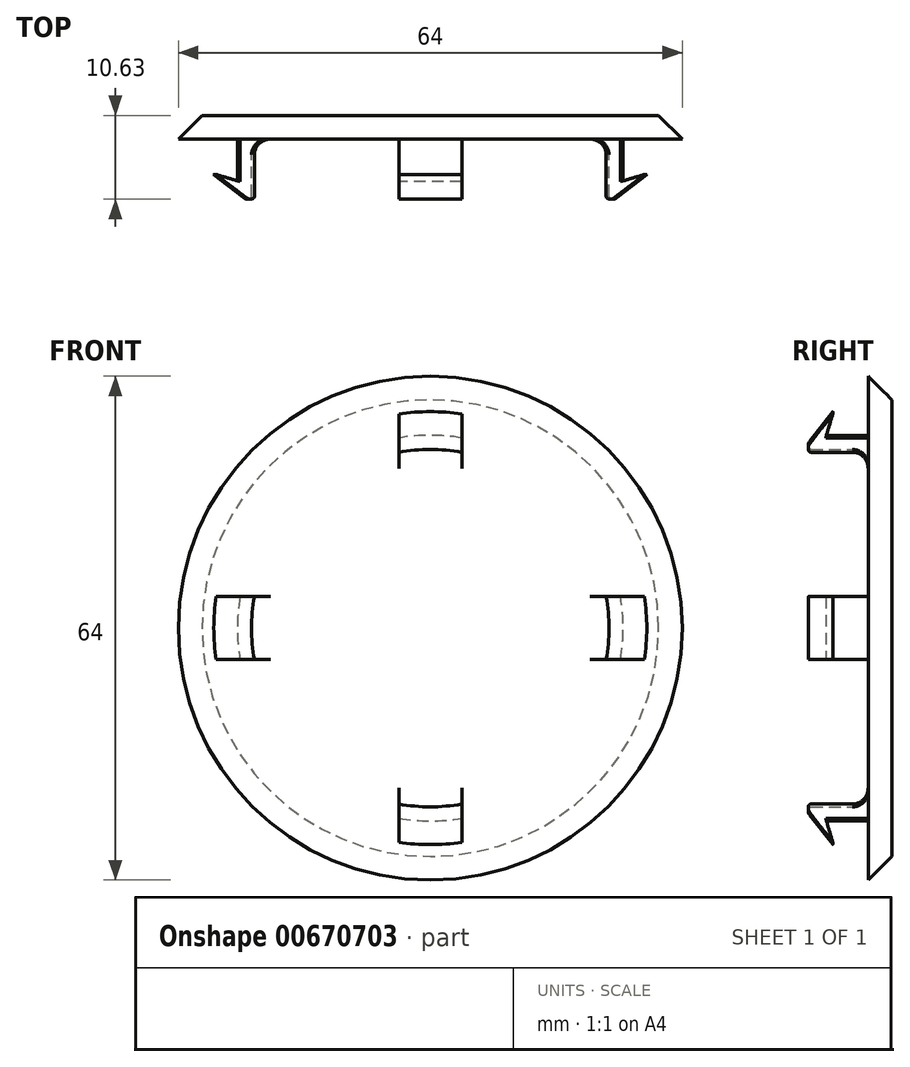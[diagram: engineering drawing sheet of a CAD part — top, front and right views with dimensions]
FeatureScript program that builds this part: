
annotation { "Feature Type Name" : "Feature", "Feature Type Description" : "" }
export const myFeature = defineFeature(function(context is Context, id is Id, definition is map)
    precondition{}
    {
        {
            var Q0;
            Q0=qCreatedBy(makeId("Top.planeOp"),FACE);
            var sketch = newSketch(context, id + "F0", { "sketchPlane" : qUnion([Q0])});
            skLineSegment(sketch, "E0", {"start": v(0, 3) * mm, "end": v(29, 3) * mm});
            skLineSegment(sketch, "E1", {"start": v(29, 3) * mm, "end": v(32, 0) * mm});
            skLineSegment(sketch, "E2", {"start": v(32, 0) * mm, "end": v(24.5, 0) * mm});
            skLineSegment(sketch, "E3", {"start": v(22.7, -7.28) * mm, "end": v(22.7, -2) * mm});
            skLineSegment(sketch, "E4", {"start": v(20.7, 0) * mm, "end": v(0, 0) * mm});
            skLineSegment(sketch, "E5", {"start": v(24.5, 0) * mm, "end": v(24.5, -3) * mm});
            skPoint(sketch, "E6.visualSharp", {"position": v(22.7, 0) * mm});
            skArc(sketch, "E6.filletArc", {"start": v(22.7, -2) * mm, "mid": v(22.11, -0.59) * mm, "end": v(20.7, 0) * mm});
            skLineSegment(sketch, "E7", {"start": v(67.9, -5) * mm, "end": v(-20.59, -5) * mm, "construction": true});
            skLineSegment(sketch, "E8", {"start": v(27.5, -4.5) * mm, "end": v(23.7, -7.45) * mm});
            skLineSegment(sketch, "E9", {"start": v(24.5, -5.4) * mm, "end": v(27.5, -4.5) * mm});
            skLineSegment(sketch, "E10", {"start": v(24.5, -3) * mm, "end": v(24.5, -5.4) * mm});
            skLineSegment(sketch, "E11", {"start": v(0, 3) * mm, "end": v(0, 0) * mm});
            skLineSegment(sketch, "E12", {"start": v(0, 22.26) * mm, "end": v(0, -28.78) * mm, "construction": true});
            skArc(sketch, "E13", {"start": v(23.7, -7.45) * mm, "mid": v(23.3, -7.62) * mm, "end": v(22.88, -7.56) * mm});
            skPoint(sketch, "E14.visualSharp", {"position": v(22.7, -7.45) * mm});
            skArc(sketch, "E14.filletArc", {"start": v(22.7, -7.28) * mm, "mid": v(22.75, -7.45) * mm, "end": v(22.88, -7.56) * mm});
            skSolve(sketch);
        }
        {
            var Q0;
            Q0=makeQuery(id+"F0.imprint","IMPRINT",FACE,{"disambiguationData":[TD([[makeQuery(id+"F0.imprint","IMPRINT",EDGE,{"derivedFrom":sQuery(id+"F0.wireOp",EDGE,"E0")}),-1.0]])]});
            var Q1;
            Q1=sQuery(id+"F0.wireOp",EDGE,"E12");
            revolve(context, id + "F1", {"entities" : qUnion([Q0]), "axis" : qUnion([Q1]), "revolveType" : RevolveType.FULL});
        }
        {
            var Q0;
            Q0=qCreatedBy(makeId("Top.planeOp"),FACE);
            var sketch = newSketch(context, id + "F2", { "sketchPlane" : qUnion([Q0])});
            skLineSegment(sketch, "E15.bottom", {"start": v(-18, 0) * mm, "end": v(-4, 0) * mm});
            skLineSegment(sketch, "E15.top", {"start": v(-22, -24.45) * mm, "end": v(-4, -24.45) * mm});
            skLineSegment(sketch, "E15.left", {"start": v(-22, -4) * mm, "end": v(-22, -24.45) * mm});
            skLineSegment(sketch, "E15.right", {"start": v(-4, 0) * mm, "end": v(-4, -24.45) * mm});
            skLineSegment(sketch, "E16.bottom", {"start": v(4, 0) * mm, "end": v(18, 0) * mm});
            skLineSegment(sketch, "E16.top", {"start": v(4, -24.45) * mm, "end": v(22, -24.45) * mm});
            skLineSegment(sketch, "E16.left", {"start": v(4, 0) * mm, "end": v(4, -24.45) * mm});
            skLineSegment(sketch, "E16.right", {"start": v(22, -4) * mm, "end": v(22, -24.45) * mm});
            skPoint(sketch, "E17.visualSharp", {"position": v(-22, 0) * mm});
            skArc(sketch, "E17.filletArc", {"start": v(-18, 0) * mm, "mid": v(-20.83, -1.17) * mm, "end": v(-22, -4) * mm});
            skPoint(sketch, "E18.visualSharp", {"position": v(22, 0) * mm});
            skArc(sketch, "E18.filletArc", {"start": v(22, -4) * mm, "mid": v(20.83, -1.17) * mm, "end": v(18, 0) * mm});
            skSolve(sketch);
        }
        {
            var Q0;
            Q0 = qSketchRegion(id + "F2", true);
            extrude(context, id + "F3", {"entities" : qUnion([Q0]), "operationType" : NewBodyOperationType.REMOVE, "endBound" : BoundingType.THROUGH_ALL, "oppositeDirection" : true, "depth" : 25 * mm, "offsetDistance" : 25 * mm, "hasSecondDirection" : true, "secondDirectionBound" : SecondDirectionBoundingType.THROUGH_ALL, "secondDirectionOppositeDirection" : false, "secondDirectionDepth" : 25 * mm});
        }
        {
            var Q0;
            Q0=qCreatedBy(makeId("Right.planeOp"),FACE);
            var sketch = newSketch(context, id + "F4", { "sketchPlane" : qUnion([Q0])});
            skLineSegment(sketch, "E19.bottom", {"start": v(0, -4) * mm, "end": v(-9.76, -4) * mm});
            skLineSegment(sketch, "E19.top", {"start": v(-4, -22) * mm, "end": v(-9.76, -22) * mm});
            skLineSegment(sketch, "E19.left", {"start": v(0, -4) * mm, "end": v(0, -18) * mm});
            skLineSegment(sketch, "E19.right", {"start": v(-9.76, -4) * mm, "end": v(-9.76, -22) * mm});
            skLineSegment(sketch, "E20.bottom", {"start": v(0, 4) * mm, "end": v(-9.75, 4) * mm});
            skLineSegment(sketch, "E20.top", {"start": v(-4, 22) * mm, "end": v(-9.75, 22) * mm});
            skLineSegment(sketch, "E20.left", {"start": v(0, 4) * mm, "end": v(0, 18) * mm});
            skLineSegment(sketch, "E20.right", {"start": v(-9.75, 4) * mm, "end": v(-9.75, 22) * mm});
            skPoint(sketch, "E21.visualSharp", {"position": v(0, 22) * mm});
            skArc(sketch, "E21.filletArc", {"start": v(0, 18) * mm, "mid": v(-1.17, 20.83) * mm, "end": v(-4, 22) * mm});
            skPoint(sketch, "E22.visualSharp", {"position": v(0, -22) * mm});
            skArc(sketch, "E22.filletArc", {"start": v(-4, -22) * mm, "mid": v(-1.17, -20.83) * mm, "end": v(0, -18) * mm});
            skSolve(sketch);
        }
        {
            var Q0;
            Q0=makeQuery(id+"F4.imprint","IMPRINT",FACE,{"disambiguationData":[TD([[makeQuery(id+"F4.imprint","IMPRINT",EDGE,{"derivedFrom":sQuery(id+"F4.wireOp",EDGE,"C3fBRqr5-fuM2-F1PP-bj7P-05VtXwCI2kac.bottom")}),1.0]])]});
            var Q1;
            Q1=makeQuery(id+"F4.imprint","IMPRINT",FACE,{"disambiguationData":[TD([[makeQuery(id+"F4.imprint","IMPRINT",EDGE,{"derivedFrom":sQuery(id+"F4.wireOp",EDGE,"AzTuuxB7-9Otc-jFpb-sgAd-WmSeQyXGKVqN.bottom")}),1.0]])]});
            var Q2;
            Q2=makeQuery(id+"F4.imprint","IMPRINT",FACE,{"disambiguationData":[TD([[makeQuery(id+"F4.imprint","IMPRINT",EDGE,{"derivedFrom":sQuery(id+"F4.wireOp",EDGE,"E20.bottom")}),-1.0]])]});
            var Q3;
            Q3=makeQuery(id+"F4.imprint","IMPRINT",FACE,{"disambiguationData":[TD([[makeQuery(id+"F4.imprint","IMPRINT",EDGE,{"derivedFrom":sQuery(id+"F4.wireOp",EDGE,"E19.bottom")}),1.0]])]});
            extrude(context, id + "F5", {"entities" : qUnion([Q0, Q1, Q2, Q3]), "operationType" : NewBodyOperationType.REMOVE, "endBound" : BoundingType.THROUGH_ALL, "oppositeDirection" : true, "depth" : 25 * mm, "offsetDistance" : 25 * mm, "hasSecondDirection" : true, "secondDirectionBound" : SecondDirectionBoundingType.THROUGH_ALL, "secondDirectionOppositeDirection" : false, "secondDirectionDepth" : 25 * mm});
        }
    });
